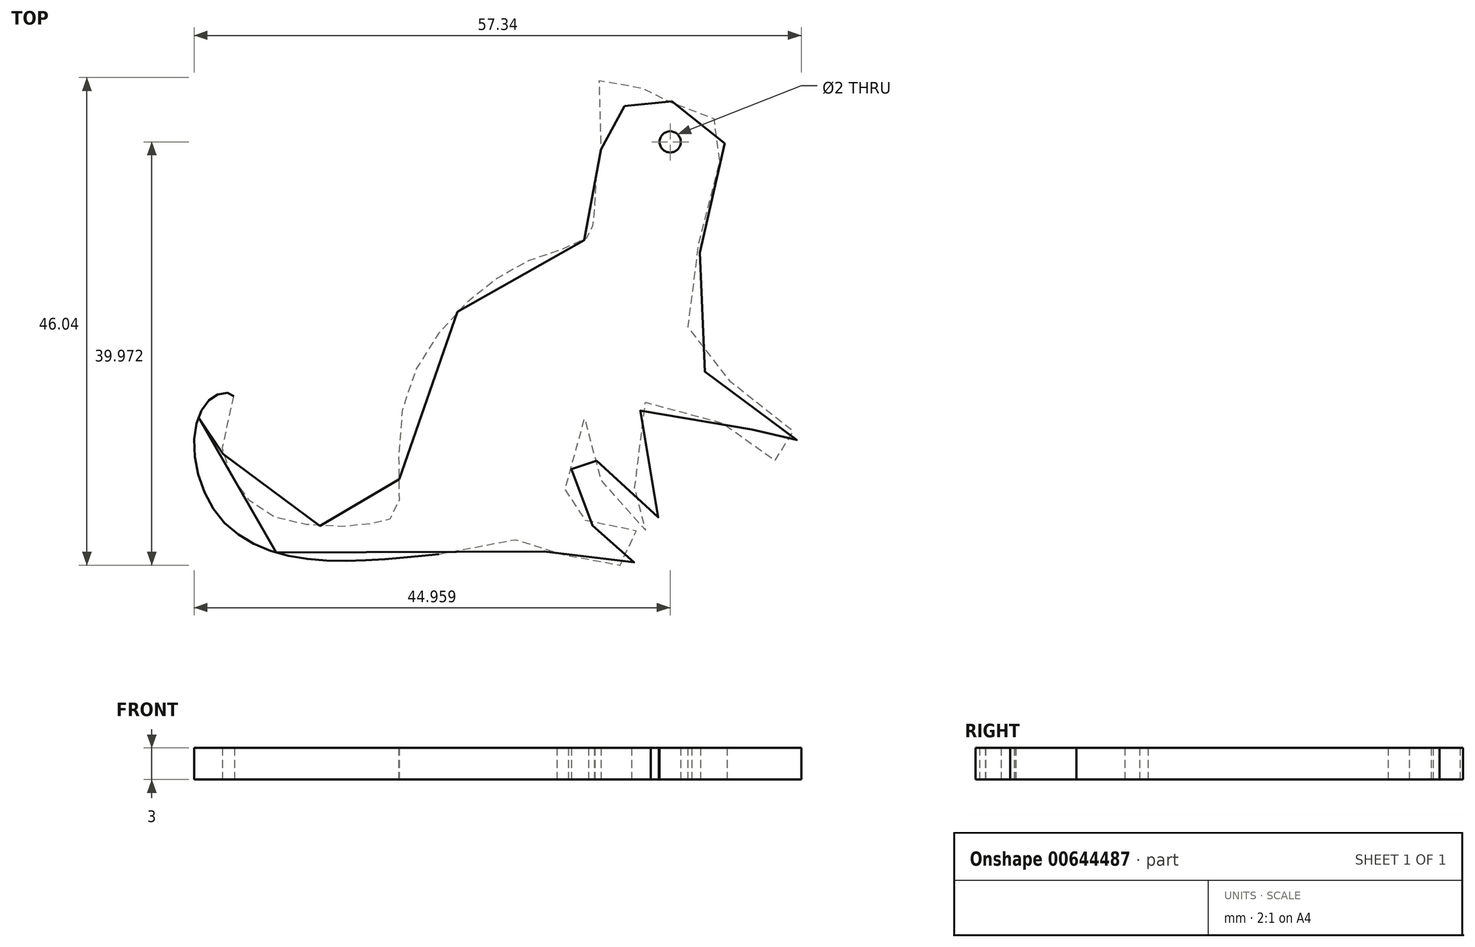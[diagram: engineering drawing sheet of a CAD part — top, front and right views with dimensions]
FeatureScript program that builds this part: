
annotation { "Feature Type Name" : "Feature", "Feature Type Description" : "" }
export const myFeature = defineFeature(function(context is Context, id is Id, definition is map)
    precondition{}
    {
        {
            var Q0;
            Q0=qCreatedBy(makeId("Top.planeOp"),FACE);
            var sketch = newSketch(context, id + "F0", { "sketchPlane" : qUnion([Q0])});
            skFitSpline(sketch, "E0", {"points": [v(-20.84, 41.13) * mm, v(-21.38, 38.25) * mm, v(-21.47, 34.19) * mm, v(-21.74, 33.74) * mm, v(-22.2, 32.74) * mm, v(-26.07, 31.21) * mm, v(-31.4, 28.41) * mm, v(-36.9, 22.73) * mm, v(-39.87, 14.52) * mm, v(-40.14, 6.77) * mm, v(-41.31, 6.04) * mm, v(-43.66, 5.6) * mm, v(-49.25, 5.77) * mm, v(-53.4, 7.4) * mm, v(-56.1, 11.1) * mm, v(-56.38, 14.52) * mm, v(-55.48, 17.77) * mm, v(-57.1, 17.95) * mm, v(-59.18, 14.43) * mm, v(-57.01, 6.59) * mm, v(-49.7, 2.62) * mm, v(-40.05, 2.53) * mm, v(-32.93, 3.43) * mm, v(-29.68, 4.24) * mm, v(-28.32, 4.15) * mm, v(-27.6, 3.7) * mm, v(-25.8, 3.07) * mm, v(-23.18, 2.8) * mm, v(-20.57, 2.62) * mm, v(-19.3, 1.9) * mm, v(-16.78, 2.7) * mm, v(-16.24, 4.33) * mm, v(-18.31, 5.32) * mm, v(-20.66, 5.68) * mm, v(-22.01, 5.68) * mm, v(-22.46, 6.31) * mm, v(-24.27, 6.68) * mm, v(-24.99, 7.22) * mm, v(-23.63, 10.55) * mm, v(-23.81, 13.8) * mm, v(-21.74, 15.97) * mm, v(-21.47, 13.8) * mm, v(-20.48, 8.75) * mm, v(-18.94, 6.13) * mm, v(-16.33, 5.23) * mm, v(-15.43, 7.04) * mm, v(-16.96, 8.2) * mm, v(-17.95, 11.28) * mm, v(-16.87, 16.96) * mm, v(-15.97, 17.32) * mm, v(-11.73, 15.6) * mm, v(-6.5, 14.61) * mm, v(-4.96, 12.36) * mm, v(-3.88, 11.55) * mm, v(-2.07, 11.64) * mm, v(-2.26, 13.44) * mm, v(-3.97, 16.5) * mm, v(-7.85, 18.94) * mm, v(-11, 20.12) * mm, v(-12.63, 23.81) * mm, v(-11.82, 27.06) * mm, v(-11.64, 32.3) * mm, v(-12, 36.71) * mm, v(-8.93, 40.95) * mm, v(-9.11, 41.59) * mm, v(-9.38, 43.2) * mm, v(-10.37, 44.11) * mm, v(-11.82, 44.65) * mm, v(-12.72, 45.37) * mm, v(-14.52, 45.55) * mm, v(-15.88, 45.2) * mm, v(-16.5, 47.9) * mm, v(-17.68, 45.01) * mm, v(-19.3, 46) * mm, v(-21.2, 47.63) * mm, v(-22.01, 46.1) * mm, v(-20.84, 41.13) * mm]});
            skSolve(sketch);
        }
        {
            var Q0;
            Q0=makeQuery(id+"F0.imprint","IMPRINT",FACE,{"disambiguationData":[TD([[makeQuery(id+"F0.imprint","IMPRINT",EDGE,{"derivedFrom":sQuery(id+"F0.wireOp",EDGE,"E0")}),1.0]])]});
            var sketch = newSketch(context, id + "F1", { "sketchPlane" : qUnion([Q0])});
            skCircle(sketch, "E1", {"center": v(-14.3, 41.83) * mm, "radius": 1.5 * mm});
            skSolve(sketch);
        }
        {
            var Q0;
            Q0=makeQuery(id+"F0.imprint","IMPRINT",FACE,{"disambiguationData":[TD([[makeQuery(id+"F0.imprint","IMPRINT",EDGE,{"derivedFrom":sQuery(id+"F0.wireOp",EDGE,"E0")}),1.0]])]});
            extrude(context, id + "F2", {"entities" : qUnion([Q0]), "depth" : 3 * mm, "offsetDistance" : 25 * mm});
        }
        {
            var Q0;
            Q0=sQuery(id+"F1.wireOp",VERTEX,"E1.center");
            var Q1;
            Q1=makeQuery(id+"F2.opExtrude","SWEPT_BODY",BODY,{"disambiguationData":[OSD([sQuery(id+"F0.wireOp",EDGE,"E0")])]});
            hole(context, id + "F3", {"style" : HoleStyle.SIMPLE, "endStyle" : HoleEndStyle.THROUGH, "oppositeDirection" : true, "holeDiameter" : 2 * mm, "majorDiameter" : 5 * mm, "isTappedThrough" : true, "tappedDepth" : 12 * mm, "tapClearance" : 3, "locations" : qUnion([Q0]), "scope" : qUnion([Q1])});
        }
    });
